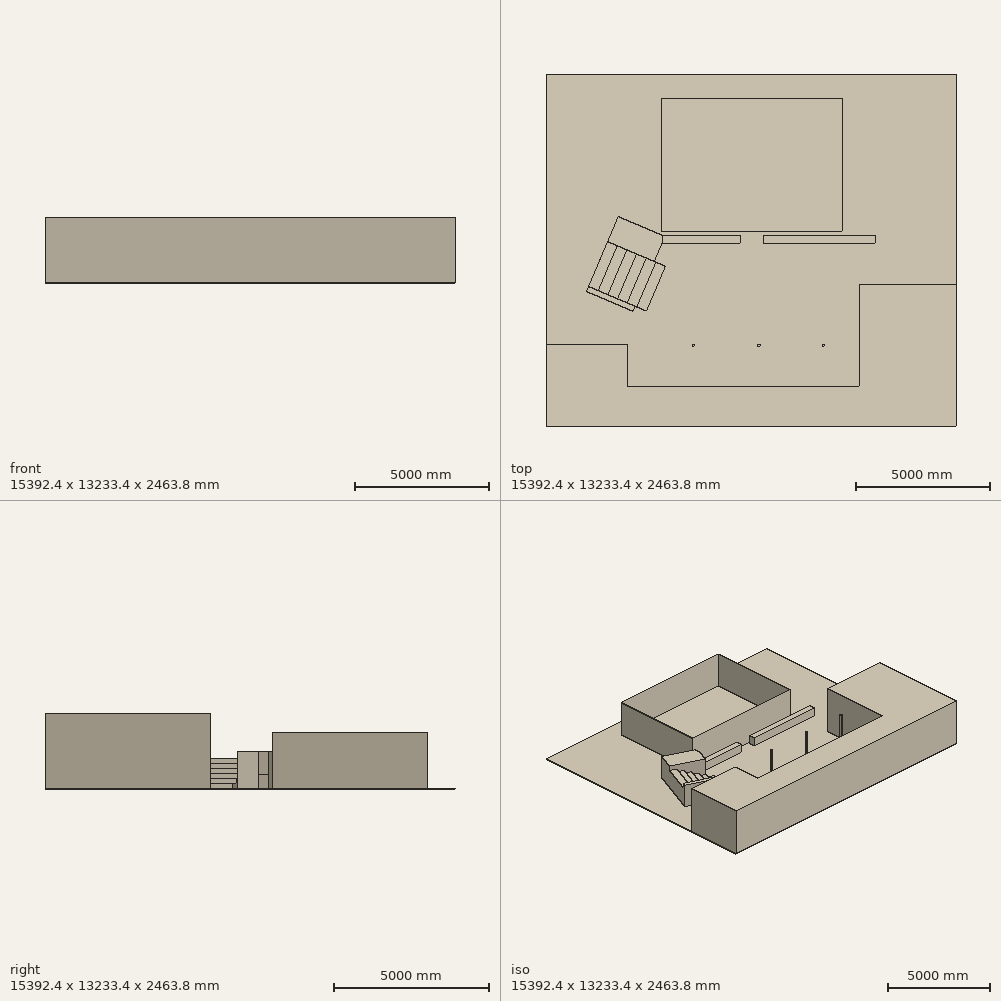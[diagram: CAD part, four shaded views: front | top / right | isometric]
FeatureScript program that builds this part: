
annotation { "Feature Type Name" : "Feature", "Feature Type Description" : "" }
export const myFeature = defineFeature(function(context is Context, id is Id, definition is map)
    precondition{}
    {
        {
            var Q0;
            Q0=qCreatedBy(makeId("Top.planeOp"),FACE);
            var sketch = newSketch(context, id + "F0", { "sketchPlane" : qUnion([Q0])});
            skLineSegment(sketch, "E0.bottom", {"start": v(444.5, 304.8) * mm, "end": v(4635.5, 304.8) * mm});
            skLineSegment(sketch, "E0.top", {"start": v(444.5, 0) * mm, "end": v(4635.5, 0) * mm});
            skLineSegment(sketch, "E0.left", {"start": v(444.5, 304.8) * mm, "end": v(444.5, 0) * mm});
            skLineSegment(sketch, "E0.right", {"start": v(4635.5, 304.8) * mm, "end": v(4635.5, 0) * mm});
            skLineSegment(sketch, "E1.bottom", {"start": v(-3365.5, 304.8) * mm, "end": v(-444.5, 304.8) * mm});
            skLineSegment(sketch, "E1.top", {"start": v(-3365.5, 0) * mm, "end": v(-444.5, 0) * mm});
            skLineSegment(sketch, "E1.left", {"start": v(-3365.5, 304.8) * mm, "end": v(-3365.5, 0) * mm});
            skLineSegment(sketch, "E1.right", {"start": v(-444.5, 304.8) * mm, "end": v(-444.5, 0) * mm});
            skLineSegment(sketch, "E2", {"start": v(-444.5, 304.8) * mm, "end": v(444.5, 304.8) * mm, "construction": true});
            skLineSegment(sketch, "E3", {"start": v(-444.5, 0) * mm, "end": v(444.5, 0) * mm, "construction": true});
            skSolve(sketch);
        }
        {
            var Q0;
            Q0 = qSketchRegion(id + "F0", true);
            extrude(context, id + "F1", {"entities" : qUnion([Q0]), "depth" : 457.2 * mm});
        }
        {
            var Q0;
            Q0=qCreatedBy(makeId("Top.planeOp"),FACE);
            var sketch = newSketch(context, id + "F2", { "sketchPlane" : qUnion([Q0])});
            skLineSegment(sketch, "E4", {"start": v(4025.9, -1549.4) * mm, "end": v(4025.9, -5359.4) * mm});
            skLineSegment(sketch, "E5", {"start": v(4025.9, -5359.4) * mm, "end": v(-4660.9, -5359.4) * mm});
            skLineSegment(sketch, "E6", {"start": v(-4660.9, -5359.4) * mm, "end": v(-4660.9, -3784.6) * mm});
            skLineSegment(sketch, "E7", {"start": v(-4660.9, -3784.6) * mm, "end": v(-7708.9, -3784.6) * mm});
            skLineSegment(sketch, "E8", {"start": v(-7708.9, -3784.6) * mm, "end": v(-7708.9, -6883.4) * mm});
            skLineSegment(sketch, "E9", {"start": v(-7708.9, -6883.4) * mm, "end": v(4635.5, -6883.4) * mm});
            skLineSegment(sketch, "E10", {"start": v(4635.5, -6883.4) * mm, "end": v(4635.5, -1549.4) * mm, "construction": true});
            skLineSegment(sketch, "E11", {"start": v(4635.5, -1549.4) * mm, "end": v(4025.9, -1549.4) * mm});
            skPoint(sketch, "E12.end.orphan", {"position": v(4635.5, 0) * mm});
            skLineSegment(sketch, "E13", {"start": v(4635.5, 0) * mm, "end": v(4635.5, -1549.4) * mm, "construction": true});
            skLineSegment(sketch, "E14", {"start": v(-4660.9, -3784.6) * mm, "end": v(4025.9, -3784.6) * mm, "construction": true});
            skLineSegment(sketch, "E15.bottom", {"start": v(-2222.5, -3784.6) * mm, "end": v(-2137.83, -3784.6) * mm});
            skLineSegment(sketch, "E15.top", {"start": v(-2222.5, -3869.27) * mm, "end": v(-2137.83, -3869.27) * mm});
            skLineSegment(sketch, "E15.left", {"start": v(-2222.5, -3784.6) * mm, "end": v(-2222.5, -3869.27) * mm});
            skLineSegment(sketch, "E15.right", {"start": v(-2137.83, -3784.6) * mm, "end": v(-2137.83, -3869.27) * mm});
            skLineSegment(sketch, "E16.bottom", {"start": v(224.37, -3784.6) * mm, "end": v(309.03, -3784.6) * mm});
            skLineSegment(sketch, "E16.top", {"start": v(224.37, -3869.27) * mm, "end": v(309.03, -3869.27) * mm});
            skLineSegment(sketch, "E16.left", {"start": v(224.37, -3784.6) * mm, "end": v(224.37, -3869.27) * mm});
            skLineSegment(sketch, "E16.right", {"start": v(309.03, -3784.6) * mm, "end": v(309.03, -3869.27) * mm});
            skLineSegment(sketch, "E17.bottom", {"start": v(2645.83, -3784.6) * mm, "end": v(2730.5, -3784.6) * mm});
            skLineSegment(sketch, "E17.top", {"start": v(2645.83, -3869.27) * mm, "end": v(2730.5, -3869.27) * mm});
            skLineSegment(sketch, "E17.left", {"start": v(2645.83, -3784.6) * mm, "end": v(2645.83, -3869.27) * mm});
            skLineSegment(sketch, "E17.right", {"start": v(2730.5, -3784.6) * mm, "end": v(2730.5, -3869.27) * mm});
            skLineSegment(sketch, "E18", {"start": v(4635.5, -1549.4) * mm, "end": v(7683.5, -1549.4) * mm});
            skLineSegment(sketch, "E19", {"start": v(7683.5, -1549.4) * mm, "end": v(7683.5, -6883.4) * mm});
            skLineSegment(sketch, "E20", {"start": v(7683.5, -6883.4) * mm, "end": v(4635.5, -6883.4) * mm});
            skSolve(sketch);
        }
        {
            var Q0;
            Q0 = qSketchRegion(id + "F2", true);
            extrude(context, id + "F3", {"entities" : qUnion([Q0]), "depth" : 2438.4 * mm});
        }
        {
            var Q0;
            Q0=qCreatedBy(makeId("Top.planeOp"),FACE);
            var sketch = newSketch(context, id + "F4", { "sketchPlane" : qUnion([Q0])});
            skLineSegment(sketch, "E21", {"start": v(-3365.5, 0) * mm, "end": v(-3655.78, -683.07) * mm});
            skLineSegment(sketch, "E22", {"start": v(-3655.78, -683.07) * mm, "end": v(-3235, -861.88) * mm});
            skLineSegment(sketch, "E23", {"start": v(-3235, -861.88) * mm, "end": v(-3950.25, -2545) * mm});
            skLineSegment(sketch, "E24", {"start": v(-3365.5, 304.8) * mm, "end": v(-3365.5, 0) * mm});
            skLineSegment(sketch, "E25", {"start": v(-4660.9, -2463.8) * mm, "end": v(-4660.9, -3784.6) * mm, "construction": true});
            skLineSegment(sketch, "E26", {"start": v(-3950.25, -2545) * mm, "end": v(-4371.04, -2366.2) * mm});
            skLineSegment(sketch, "E27", {"start": v(-4371.04, -2366.2) * mm, "end": v(-4450.5, -2553.2) * mm});
            skLineSegment(sketch, "E28", {"start": v(-4450.5, -2553.2) * mm, "end": v(-4660.9, -2463.8) * mm});
            skLineSegment(sketch, "E29", {"start": v(-4660.9, -2463.8) * mm, "end": v(-6203.77, -1808.15) * mm});
            skLineSegment(sketch, "E30", {"start": v(-6203.77, -1808.15) * mm, "end": v(-5009.04, 1003.24) * mm});
            skLineSegment(sketch, "E31", {"start": v(-5009.04, 1003.24) * mm, "end": v(-3365.5, 304.8) * mm});
            skSolve(sketch);
        }
        {
            var Q0;
            Q0 = qSketchRegion(id + "F4", true);
            extrude(context, id + "F5", {"entities" : qUnion([Q0]), "operationType" : NewBodyOperationType.ADD, "depth" : 1219.2 * mm});
        }
        {
            var Q0;
            Q0=makeQuery(id+"F5.opExtrude","SWEPT_FACE",FACE,{"disambiguationData":[OSD([sQuery(id+"F4.wireOp",EDGE,"E22")])]});
            var sketch = newSketch(context, id + "F6", { "sketchPlane" : qUnion([Q0])});
            skLineSegment(sketch, "E32", {"start": v(2640.22, 0) * mm, "end": v(2640.22, 160.87) * mm, "construction": true});
            skLineSegment(sketch, "E33", {"start": v(2640.22, 160.87) * mm, "end": v(3033.92, 160.87) * mm});
            skLineSegment(sketch, "E34", {"start": v(3033.92, 160.87) * mm, "end": v(3033.92, 321.73) * mm});
            skLineSegment(sketch, "E35", {"start": v(3033.92, 321.73) * mm, "end": v(3427.62, 321.73) * mm});
            skLineSegment(sketch, "E36", {"start": v(3427.62, 321.73) * mm, "end": v(3427.62, 482.6) * mm});
            skLineSegment(sketch, "E37", {"start": v(3427.62, 482.6) * mm, "end": v(3821.32, 482.6) * mm});
            skLineSegment(sketch, "E38", {"start": v(3821.32, 482.6) * mm, "end": v(3821.32, 643.47) * mm});
            skLineSegment(sketch, "E39", {"start": v(3821.32, 643.47) * mm, "end": v(4215.02, 643.47) * mm});
            skLineSegment(sketch, "E40", {"start": v(4215.02, 643.47) * mm, "end": v(4215.02, 804.33) * mm});
            skLineSegment(sketch, "E41", {"start": v(4215.02, 804.33) * mm, "end": v(4608.72, 804.33) * mm});
            skLineSegment(sketch, "E42", {"start": v(4608.72, 804.33) * mm, "end": v(4608.72, 965.2) * mm});
            skLineSegment(sketch, "E43", {"start": v(4608.72, 965.2) * mm, "end": v(5002.42, 965.2) * mm});
            skLineSegment(sketch, "E44", {"start": v(5002.42, 965.2) * mm, "end": v(5002.42, 0) * mm, "construction": true});
            skLineSegment(sketch, "E45", {"start": v(5002.42, 0) * mm, "end": v(2640.22, 0) * mm, "construction": true});
            skLineSegment(sketch, "E46", {"start": v(2640.22, 160.87) * mm, "end": v(2640.22, 1219.2) * mm});
            skLineSegment(sketch, "E47", {"start": v(2640.22, 1219.2) * mm, "end": v(5002.42, 1219.2) * mm});
            skLineSegment(sketch, "E48", {"start": v(5002.42, 1219.2) * mm, "end": v(5002.42, 965.2) * mm});
            skSolve(sketch);
        }
        {
            var Q0;
            Q0 = qSketchRegion(id + "F6", true);
            extrude(context, id + "F7", {"entities" : qUnion([Q0]), "operationType" : NewBodyOperationType.REMOVE, "oppositeDirection" : true, "depth" : 1828.8 * mm});
        }
        {
            var Q0;
            Q0=qCreatedBy(makeId("Top.planeOp"),FACE);
            var sketch = newSketch(context, id + "F8", { "sketchPlane" : qUnion([Q0])});
            skLineSegment(sketch, "E49.bottom", {"start": v(-7708.9, 6350) * mm, "end": v(7683.5, 6350) * mm});
            skLineSegment(sketch, "E49.top", {"start": v(-7708.9, -6883.4) * mm, "end": v(7683.5, -6883.4) * mm});
            skLineSegment(sketch, "E49.left", {"start": v(-7708.9, 6350) * mm, "end": v(-7708.9, -6883.4) * mm});
            skLineSegment(sketch, "E49.right", {"start": v(7683.5, 6350) * mm, "end": v(7683.5, -6883.4) * mm});
            skSolve(sketch);
        }
        {
            var Q0;
            Q0 = qSketchRegion(id + "F8", true);
            extrude(context, id + "F9", {"entities" : qUnion([Q0]), "oppositeDirection" : true, "depth" : 25.4 * mm});
        }
        {
            var Q0;
            Q0=qCreatedBy(makeId("Top.planeOp"),FACE);
            var sketch = newSketch(context, id + "F10", { "sketchPlane" : qUnion([Q0])});
            skLineSegment(sketch, "E50.bottom", {"start": v(-3403.6, 5435.6) * mm, "end": v(3403.6, 5435.6) * mm});
            skLineSegment(sketch, "E50.top", {"start": v(-3403.6, 431.8) * mm, "end": v(3403.6, 431.8) * mm});
            skLineSegment(sketch, "E50.left", {"start": v(-3403.6, 5435.6) * mm, "end": v(-3403.6, 431.8) * mm});
            skLineSegment(sketch, "E50.right", {"start": v(3403.6, 5435.6) * mm, "end": v(3403.6, 431.8) * mm});
            skLineSegment(sketch, "E51", {"start": v(0, 0) * mm, "end": v(0, 5435.6) * mm, "construction": true});
            skLineSegment(sketch, "E52.bottom", {"start": v(-3398.52, 5430.52) * mm, "end": v(3398.52, 5430.52) * mm});
            skLineSegment(sketch, "E52.top", {"start": v(-3398.52, 436.88) * mm, "end": v(3398.52, 436.88) * mm});
            skLineSegment(sketch, "E52.left", {"start": v(-3398.52, 5430.52) * mm, "end": v(-3398.52, 436.88) * mm});
            skLineSegment(sketch, "E52.right", {"start": v(3398.52, 5430.52) * mm, "end": v(3398.52, 436.88) * mm});
            skSolve(sketch);
        }
        {
            var Q0;
            Q0 = qSketchRegion(id + "F10", true);
            extrude(context, id + "F11", {"entities" : qUnion([Q0]), "operationType" : NewBodyOperationType.ADD, "depth" : 1828.8 * mm});
        }
    });
